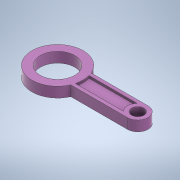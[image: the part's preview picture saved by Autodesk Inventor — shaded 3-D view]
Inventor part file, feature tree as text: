
AUTODESK INVENTOR PART (.ipt)
format: ipt  version: 2022 (Build 260153000, 153)  size: 155,648 bytes
history: native  units: mm
features: extrude x4, sketch x3, plane x1
ambient origin geometry x8: Origin, YZ Plane, XZ Plane, XY Plane, X Axis, Y Axis, Z Axis, Center Point
bodies: 实体1 (feature_tree)
feature tree (8):
  extrude  "拉伸1"  Depth=30.0mm
  plane  "工作平面1"
  extrude  "拉伸2"  Depth=12.0mm
  sketch  "草图3"  dims[d5=12.0mm d6=2.0mm d7=3.5mm d8=35.0mm d9=0.0mm d10=7.2mm d11=35.0mm d12=0.0mm d13=6.0mm d14=0.0mm]
  extrude  "拉伸3"  Depth=2.0mm
  extrude  "拉伸4"  Depth=3.5mm
  sketch  "草图1"  dims[d0=20.2mm d1=30.0mm]
  sketch  "草图2"  dims[d2=6.0mm d3=0.0mm d4=12.0mm]
